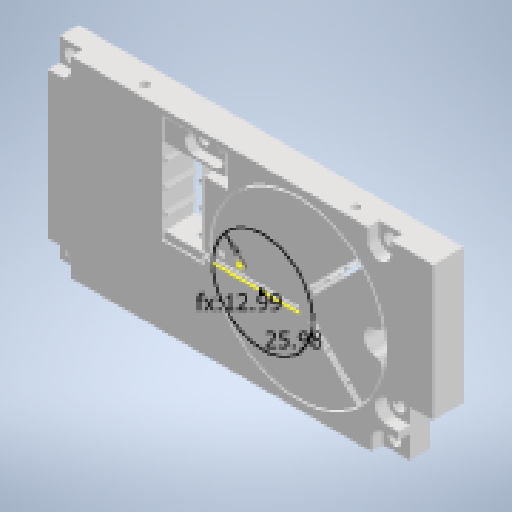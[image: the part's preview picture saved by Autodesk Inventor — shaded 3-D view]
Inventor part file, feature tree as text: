
AUTODESK INVENTOR PART (.ipt)
format: ipt  version: 2023 (Build 270158000, 158)  size: 752,128 bytes
history: native  units: mm
features: extrude x13, sketch x12, reference x5, other x5, fillet x1
ambient origin geometry x8: Origin, YZ Plane, XZ Plane, XY Plane, X Axis, Y Axis, Z Axis, Center Point
bodies: Solid1 (feature_tree)
feature tree (36):
  extrude  "Extrusion1"  Depth=8.0mm
  extrude  "Extrusion2"  Depth=15.0mm TaperAngle=0.0deg
  extrude  "Extrusion3"  Depth=15.0mm
  fillet  "Fillet1"  Radius=1.6mm
  extrude  "Extrusion4"  Depth=45.0mm
  extrude  "Extrusion5"  TaperAngle=45.0deg  [1 undecoded]
  extrude  "Extrusion6"  Depth=10.0mm
  extrude  "Extrusion7"  Depth=1.0mm
  extrude  "Extrusion8"  Depth=1.0mm
  extrude  "Extrusion9"  Depth=1.0mm
  extrude  "Extrusion10"  Depth=0.1mm
  extrude  "Extrusion11"  Depth=8.0mm TaperAngle=0.0deg
  extrude  "Extrusion12"  Depth=8.61mm
  extrude  "Extrusion13"  Depth=8.61mm
  sketch  "Sketch1"  dims[d0=8.0mm d1=0.0mm d2=9.0mm]
  reference  "Reference1"
  sketch  "Sketch2"  dims[d3=15.0mm d4=9.0mm d5=0.0mm]
  sketch  "Sketch3"  dims[d6=15.0mm d7=40.0mm d8=1.6mm]
  sketch  "Sketch4"  dims[d9=6.0mm d10=45.0mm]
  sketch  "Sketch5"  dims[d11=20.0mm d12=45.0deg]
  sketch  "Sketch8"  dims[d13=45.0deg d14=10.0mm]
  sketch  "Sketch10"  dims[d15=46.0mm d16=1.0mm]
  sketch  "Sketch11"  dims[d17=1.0mm d18=1.0mm]
  sketch  "Sketch12"  dims[d19=1.0mm d20=0.05mm]
  reference  "Reference6"
  reference  "Reference7"
  sketch  "Sketch13"  dims[d21=0.1mm d22=0.1mm]
  reference  "Reference10"
  reference  "Reference11"
  sketch  "Sketch14"  dims[d23=0.05mm d24=8.0mm d25=0.0mm]
  sketch  "Sketch15"  dims[d26=2.0mm d33=2.65mm d34=0.4mm d35=0.5mm d36=0.5mm d37=20.0mm d38=1.75mm d39=1.6mm d40=25.0mm d41=0.0mm d42=0.5mm d43=0.5mm d44=0.5mm d45=0.5mm d47=1.5mm d48=0.0mm d49=0.1mm d50=0.1mm d51=0.5mm d52=0.5mm d53=0.5mm d54=18.0mm d56=0.0mm d57=1.5mm d58=0.1mm d59=8.0mm d60=0.0mm d61=8.0mm d62=0.0mm d63=16.0mm d64=2.7mm d65=2.7mm d66=8.0mm d67=0.0mm d68=3.0mm d69=14.0mm d70=3.0mm d72=3.0mm d73=3.4mm d74=3.4mm d75=3.4mm d76=3.0mm d77=3.0mm d78=3.0mm d79=4.0mm d80=3.4mm d81=3.0mm d82=3.4mm d83=11.0mm d84=8.0mm d85=0.0mm d86=6.0mm d87=6.0mm d88=6.0mm d89=6.0mm d90=6.0mm d91=3.0mm d92=0.0mm d93=5.0mm d94=5.0mm d95=2.5mm d96=0.0mm d97=7.0mm d98=0.0mm d99=2.05mm d100=2.75mm d101=2.05mm d102=2.05mm d103=2.05mm d104=2.05mm d105=2.05mm d106=7.0mm d107=0.0mm d108=10.0mm d109=23.0mm d110=55.0mm d111=55.0mm d112=2.05mm d113=23.0mm d114=55.0mm d116=5.0mm d117=2.0mm d118=5.0mm d119=2.0mm d120=5.0mm d121=2.0mm d122=5.0mm d123=2.0mm d125=1.0mm d126=1.0mm d127=2.1mm d129=2.0mm d130=2.0mm d132=2.1mm d134=2.0mm d135=2.0mm d136=2.0mm d137=2.0mm d138=2.0mm d139=2.1mm d140=2.1mm d141=4.0mm d142=4.0mm d143=3.0mm d144=4.0mm d145=3.0mm d146=4.0mm d148=2.1mm d150=2.100022mm d151=2.699978mm d152=2.0mm d153=2.0mm d154=10.0mm d155=0.0mm d156=5.0mm d157=3.0mm d164=19.0mm d173=10.0mm d174=0.0mm d175=4.0mm d176=4.0mm d180=8.61mm d181=8.61mm d182=3.5mm d183=3.5mm d184=0.0mm]
  other  "<userpath>\ClawdDrive\Objet3D\IminaProbe\V3Roue\RoueV3.iam"
  other  "RoueV3.iam"
  other  "RoueV3PartB:1"
  other  "DifferentialLinearActuator:13"
  other  "DifferentialLinearActuator:14"
note: 1 required parameter value undecoded (feature->parameter linkage not recoverable at this tier; creation-order binding heuristic only, values carry confidence <= 0.55)
